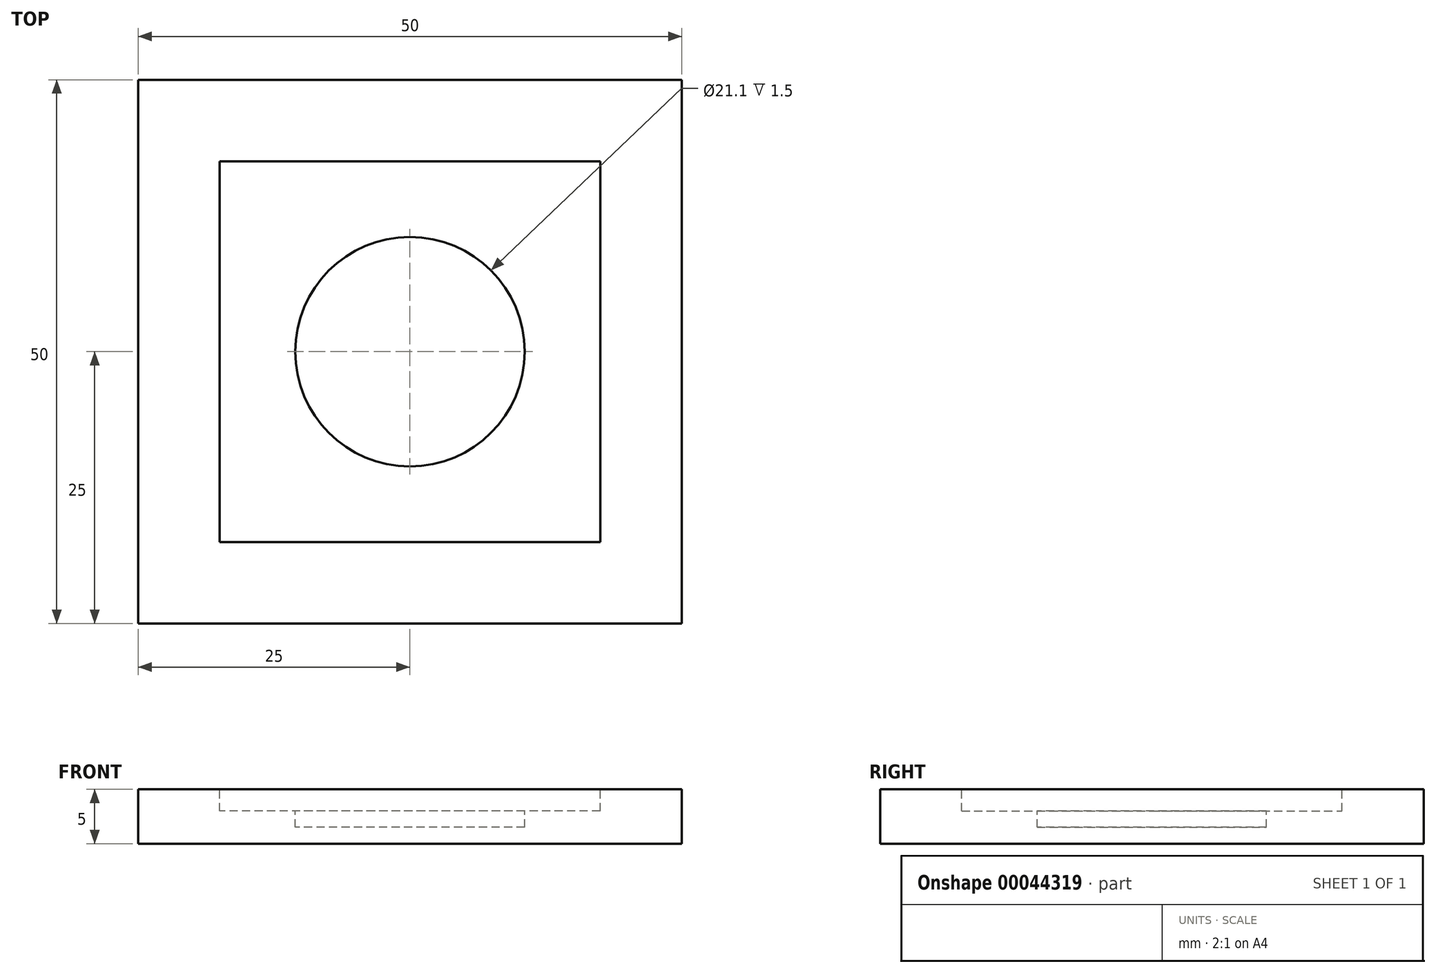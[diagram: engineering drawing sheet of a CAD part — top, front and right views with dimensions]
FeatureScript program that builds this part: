
annotation { "Feature Type Name" : "Feature", "Feature Type Description" : "" }
export const myFeature = defineFeature(function(context is Context, id is Id, definition is map)
    precondition{}
    {
        {
            var Q0;
            Q0=qCreatedBy(makeId("Top.planeOp"),FACE);
            var sketch = newSketch(context, id + "F0", { "sketchPlane" : qUnion([Q0])});
            skLineSegment(sketch, "E0.bottom", {"start": v(25, -25) * mm, "end": v(-25, -25) * mm});
            skLineSegment(sketch, "E0.top", {"start": v(25, 25) * mm, "end": v(-25, 25) * mm});
            skLineSegment(sketch, "E0.left", {"start": v(25, -25) * mm, "end": v(25, 25) * mm});
            skLineSegment(sketch, "E0.right", {"start": v(-25, -25) * mm, "end": v(-25, 25) * mm});
            skPoint(sketch, "E0.middle", {"position": v(0, 0) * mm});
            skCircle(sketch, "E1", {"center": v(0, 0) * mm, "radius": 10.55 * mm});
            skLineSegment(sketch, "E2.bottom", {"start": v(17.5, -17.5) * mm, "end": v(-17.5, -17.5) * mm});
            skLineSegment(sketch, "E2.top", {"start": v(17.5, 17.5) * mm, "end": v(-17.5, 17.5) * mm});
            skLineSegment(sketch, "E2.left", {"start": v(17.5, -17.5) * mm, "end": v(17.5, 17.5) * mm});
            skLineSegment(sketch, "E2.right", {"start": v(-17.5, -17.5) * mm, "end": v(-17.5, 17.5) * mm});
            skSolve(sketch);
        }
        {
            var Q0;
            Q0 = qSketchRegion(id + "F0", true);
            var Q1;
            Q1=makeQuery(id+"F0.imprint","IMPRINT",FACE,{"disambiguationData":[TD([[makeQuery(id+"F0.imprint","IMPRINT",EDGE,{"derivedFrom":sQuery(id+"F0.wireOp",EDGE,"E1")}),1.0]])]});
            var Q2;
            Q2=makeQuery(id+"F0.imprint","IMPRINT",FACE,{"disambiguationData":[TD([[makeQuery(id+"F0.imprint","IMPRINT",EDGE,{"derivedFrom":sQuery(id+"F0.wireOp",EDGE,"E1")}),-1.0]])]});
            extrude(context, id + "F1", {"entities" : qUnion([Q0, Q1, Q2]), "depth" : 5 * mm});
        }
        {
            var Q0;
            Q0=makeQuery(id+"F1.opExtrude","CAP_FACE",FACE,{"disambiguationData":[OSD([sQuery(id+"F0.wireOp",EDGE,"E0.bottom"),sQuery(id+"F0.wireOp",EDGE,"E0.top"),sQuery(id+"F0.wireOp",EDGE,"E0.left"),sQuery(id+"F0.wireOp",EDGE,"E0.right")])],"isStart":false});
            var sketch = newSketch(context, id + "F2", { "sketchPlane" : qUnion([Q0])});
            skCircle(sketch, "E3.0", {"center": v(0, 0) * mm, "radius": 10.55 * mm});
            skLineSegment(sketch, "E3.1", {"start": v(17.5, -17.5) * mm, "end": v(-17.5, -17.5) * mm});
            skLineSegment(sketch, "E3.2", {"start": v(-17.5, -17.5) * mm, "end": v(-17.5, 17.5) * mm});
            skLineSegment(sketch, "E4.0", {"start": v(17.5, 17.5) * mm, "end": v(-17.5, 17.5) * mm});
            skLineSegment(sketch, "E5.0", {"start": v(17.5, -17.5) * mm, "end": v(17.5, 17.5) * mm});
            skSolve(sketch);
        }
        {
            var Q0;
            Q0=makeQuery(id+"F2.imprint","IMPRINT",FACE,{"disambiguationData":[TD([[makeQuery(id+"F2.imprint","IMPRINT",EDGE,{"derivedFrom":sQuery(id+"F2.wireOp",EDGE,"E3.0")}),-1.0]])]});
            var Q1;
            Q1=makeQuery(id+"F2.imprint","IMPRINT",FACE,{"disambiguationData":[TD([[makeQuery(id+"F2.imprint","IMPRINT",EDGE,{"derivedFrom":sQuery(id+"F2.wireOp",EDGE,"E3.0")}),1.0]])]});
            extrude(context, id + "F3", {"entities" : qUnion([Q0, Q1]), "operationType" : NewBodyOperationType.REMOVE, "oppositeDirection" : true, "depth" : 2 * mm});
        }
        {
            var Q0;
            Q0=makeQuery(id+"F2.imprint","IMPRINT",FACE,{"disambiguationData":[TD([[makeQuery(id+"F2.imprint","IMPRINT",EDGE,{"derivedFrom":sQuery(id+"F2.wireOp",EDGE,"E3.0")}),1.0]])]});
            extrude(context, id + "F4", {"entities" : qUnion([Q0]), "operationType" : NewBodyOperationType.REMOVE, "oppositeDirection" : true, "depth" : 3.5 * mm});
        }
    });
